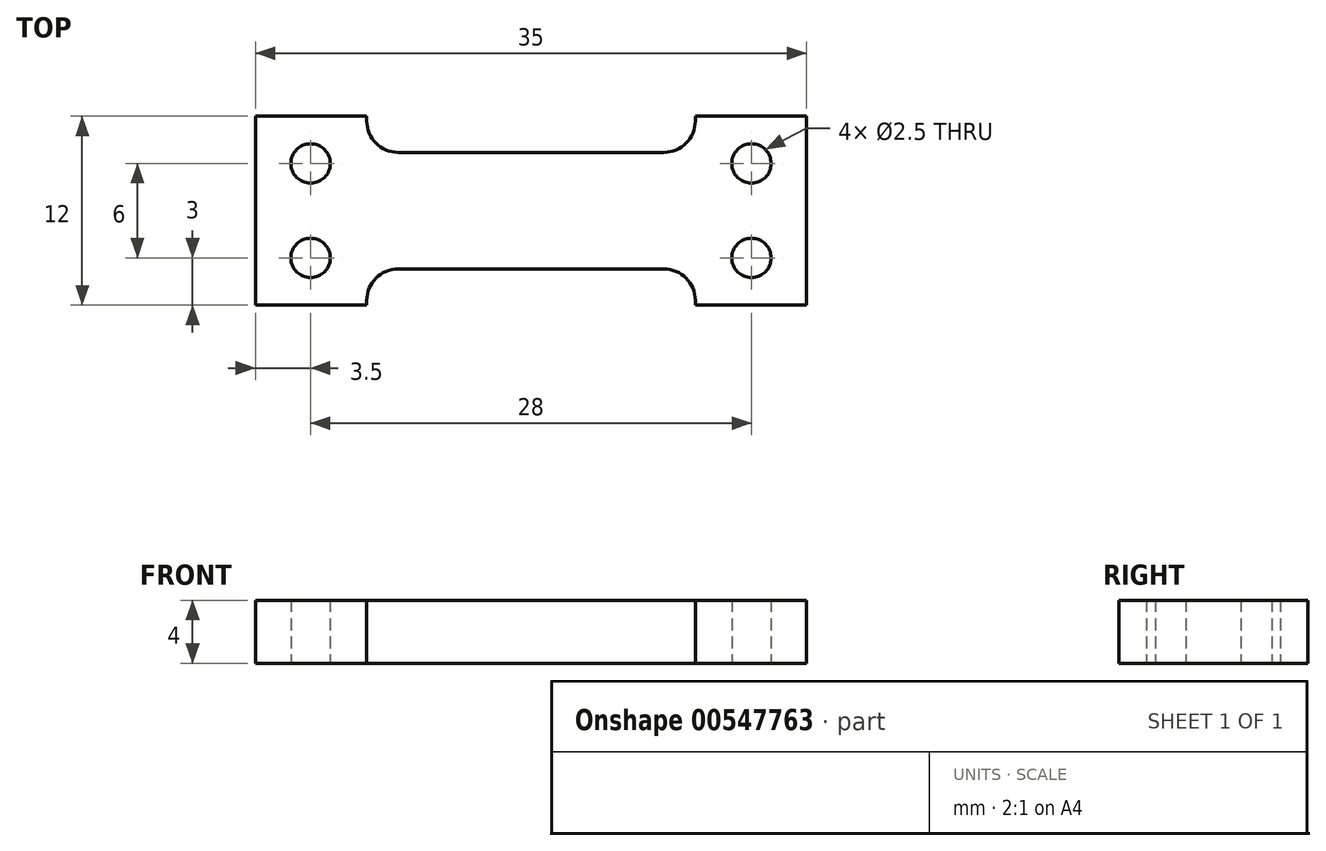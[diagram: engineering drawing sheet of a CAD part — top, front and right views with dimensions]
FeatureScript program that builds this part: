
annotation { "Feature Type Name" : "Feature", "Feature Type Description" : "" }
export const myFeature = defineFeature(function(context is Context, id is Id, definition is map)
    precondition{}
    {
        {
            var Q0;
            Q0=qCreatedBy(makeId("Top.planeOp"),FACE);
            var sketch = newSketch(context, id + "F0", { "sketchPlane" : qUnion([Q0])});
            skLineSegment(sketch, "E0.right", {"start": v(-17.5, -6) * mm, "end": v(-17.5, 0) * mm});
            skPoint(sketch, "E0.middle", {"position": v(0, 0) * mm});
            skCircle(sketch, "E1", {"center": v(-14, -3) * mm, "radius": 1.25 * mm});
            skLineSegment(sketch, "E2", {"start": v(-20.85, 0) * mm, "end": v(22.17, 0) * mm, "construction": true});
            skLineSegment(sketch, "E3", {"start": v(0, 9.83) * mm, "end": v(0, -14.57) * mm, "construction": true});
            skCircle(sketch, "E4.MirrorC", {"center": v(-14, 3) * mm, "radius": 1.25 * mm});
            skCircle(sketch, "E5.MirrorC", {"center": v(14, -3) * mm, "radius": 1.25 * mm});
            skCircle(sketch, "E6.MirrorC", {"center": v(14, 3) * mm, "radius": 1.25 * mm});
            skLineSegment(sketch, "E7", {"start": v(-17.5, -6) * mm, "end": v(-10.44, -6) * mm});
            skLineSegment(sketch, "E8", {"start": v(-10.44, -6) * mm, "end": v(-10.44, -5.7) * mm});
            skLineSegment(sketch, "E9", {"start": v(-8.44, -3.7) * mm, "end": v(-1.49, -3.7) * mm});
            skLineSegment(sketch, "E10", {"start": v(-1.49, -3.7) * mm, "end": v(0, -3.7) * mm});
            skPoint(sketch, "E11.visualSharp", {"position": v(-10.44, -3.7) * mm});
            skArc(sketch, "E11.filletArc", {"start": v(-8.44, -3.7) * mm, "mid": v(-9.85, -4.29) * mm, "end": v(-10.44, -5.7) * mm});
            skLineSegment(sketch, "E12.MirrorCS", {"start": v(-1.49, 3.7) * mm, "end": v(0, 3.7) * mm});
            skLineSegment(sketch, "E13.MirrorCS", {"start": v(-8.44, 3.7) * mm, "end": v(-1.49, 3.7) * mm});
            skLineSegment(sketch, "E14.MirrorCS", {"start": v(-10.44, 6) * mm, "end": v(-10.44, 5.7) * mm});
            skArc(sketch, "E15.MirrorCS", {"start": v(-8.44, 3.7) * mm, "mid": v(-9.85, 4.29) * mm, "end": v(-10.44, 5.7) * mm});
            skLineSegment(sketch, "E16.MirrorCS", {"start": v(-17.5, 6) * mm, "end": v(-17.5, 0) * mm});
            skLineSegment(sketch, "E17.MirrorCS", {"start": v(-17.5, 6) * mm, "end": v(-10.44, 6) * mm});
            skLineSegment(sketch, "E18.MirrorCS", {"start": v(10.44, 6) * mm, "end": v(10.44, 5.7) * mm});
            skArc(sketch, "E19.MirrorCS", {"start": v(8.44, 3.7) * mm, "mid": v(9.85, 4.29) * mm, "end": v(10.44, 5.7) * mm});
            skLineSegment(sketch, "E20.MirrorCS", {"start": v(8.44, 3.7) * mm, "end": v(1.49, 3.7) * mm});
            skLineSegment(sketch, "E21.MirrorCS", {"start": v(1.49, 3.7) * mm, "end": v(0, 3.7) * mm});
            skLineSegment(sketch, "E22.MirrorCS", {"start": v(1.49, -3.7) * mm, "end": v(0, -3.7) * mm});
            skLineSegment(sketch, "E23.MirrorCS", {"start": v(8.44, -3.7) * mm, "end": v(1.49, -3.7) * mm});
            skArc(sketch, "E24.MirrorCS", {"start": v(8.44, -3.7) * mm, "mid": v(9.85, -4.29) * mm, "end": v(10.44, -5.7) * mm});
            skLineSegment(sketch, "E25.MirrorCS", {"start": v(10.44, -6) * mm, "end": v(10.44, -5.7) * mm});
            skLineSegment(sketch, "E26.MirrorCS", {"start": v(17.5, -6) * mm, "end": v(10.44, -6) * mm});
            skLineSegment(sketch, "E27.MirrorCS", {"start": v(17.5, 6) * mm, "end": v(10.44, 6) * mm});
            skLineSegment(sketch, "E28.MirrorCS", {"start": v(17.5, -6) * mm, "end": v(17.5, 0) * mm});
            skLineSegment(sketch, "E29.MirrorCS", {"start": v(17.5, 6) * mm, "end": v(17.5, 0) * mm});
            skSolve(sketch);
        }
        {
            var Q0;
            Q0 = qSketchRegion(id + "F0", true);
            extrude(context, id + "F1", {"entities" : qUnion([Q0]), "depth" : 4 * mm, "offsetDistance" : 25 * mm});
        }
    });
